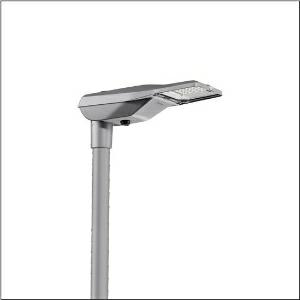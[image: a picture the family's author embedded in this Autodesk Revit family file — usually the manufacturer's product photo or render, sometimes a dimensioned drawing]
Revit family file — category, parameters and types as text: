
# Revit family: streetlight_sl_21_iq_micro___p0_8a_5xe1u31u08db_b9e4
name_source: partatom
category: Lighting Fixtures
units: mm (PartAtom-declared; Revit-internal decimal feet)

## family parameters
Cut with Voids When Loaded = No
Host = Face
Light Source = No
Part Type = Normal
Room Calculation Point = No
Round Connector Dimension = Use Diameter
Shared = No

## types (1)
- --- (1 x LED, 5130 lm, 39.1 W, 3000K)
    Apparent Load = 39 VA
    CIE Flux Codes = 33 69 96 100 100
    Color Rendering = 70
    Color Temperature = 3000K
    Default Elevation = 1800 mm
    Description = Streetlight SL 21 iQ micro, mast luminaire, primary light control with lens, of PMMA, primary optical cover: cover, of toughened safety glass, transparent, light distribution: P0.8a, light emission: direct distribution, primary light characteristic: asymmetric, installation type: post-top, side-entry, LED, High Power LED, rated luminous flux: 5.130lm, luminous efficacy: 131lm/W, light colour: 730, colour temperature: 3000K, control gear: iQ-Street Remote, D4i with power reduction, control: pre-setting: logarithmic dimming characteristic, Street-Remote, Auto-Match, Temp-Guard, Lumen-Switch, Night-Set, Smart-Wire, Light-Fading, Desk-Remote (wireless, voltage-free reading and setting of iQ features in the workshop via application-optimized NFC function/RFID function), optimised constant luminous flux control (CLO 2.0), mains connection: 220..240V, AC, 50/60Hz, start of lifetime: 39W, end of service life: 41W, reduction: 17W, luminaire housing, of diecast aluminium, powder-coated, SITECO metallic grey (DB 702S), corrosivity category C5 high according to DIN EN ISO 12944, please order mast flange separately, inclination adjustable: 0°, 5°, 10°, 15°, sealing non-destructively replaceable, multi-level sealing system, length: 528mm, width: 235mm, height: 110mm, mast flange for spigot size: 42mm (side-entry): 5XC10008XM4, 60/48mm (side-entry/post-top): 5XC10108XM2, 76/60mm (side-entry/post-top): 5XC10108XM1, mounting height: 4..8m, Smart Interface below, protection rating (complete): IP66, insulation class (complete): insulation class II (safety insulation), certification: CE, ENEC, ENEC+, VDE, impact resistance: IK10, permissible operating ambient temperature for outdoor applications: -40..+50°C, standard-compliant lighting for roads and squares, packaging unit: 1 piece

Light Distribution: P0.8a
    Height = 110 mm
    Lamp = 1 x LED
    Lamp Light Flux = 5130 lm
    Lamp Power = 39.1 W
    Lamp count = 1
    Length = 528 mm
    Luminous efficacy = 131 lm/W
    Manufacturer = Siteco
    ModVariant = No
    Model = 5XE1U31U08DB
    Number of Poles = 1
    OnlyDefault = Yes
    Power Factor = 1
    Product Name = Streetlight SL 21 iQ micro | P0.8a
    Product group = mast luminaire | pylon top
    ProductGroupID = 6100
    Protection Class = Protection class II
    Protection Degree = IP 66
    RLX_Detail_Level = 1
    RLX_Emergency_Light_Flux = 0 lm
    RLX_Emergency_Type = 0
    RLX_Emergency_Type_DB = No
    RlxData = <blob elided: 98877 chars, md5=dbcf8ff1>
    Socket = socket
    Standby Power = 0 W
    System Light Flux = 5130 lm
    System Power = 39 W
    Type Comments = factory setting: luminous flux: 100 % | dim-lin: 254 | 765 mA
    Type Image = l_1277290.jpg
    URL = http://relux.com
    VarID = @adj_082073
    Voltage = 0 V
    Weight = 0.00 kg
    Width = 235 mm

## geometry (parser evidence)
native form markers: Blend x4, Sweep x9
no freeform markers — native parametric forms only
